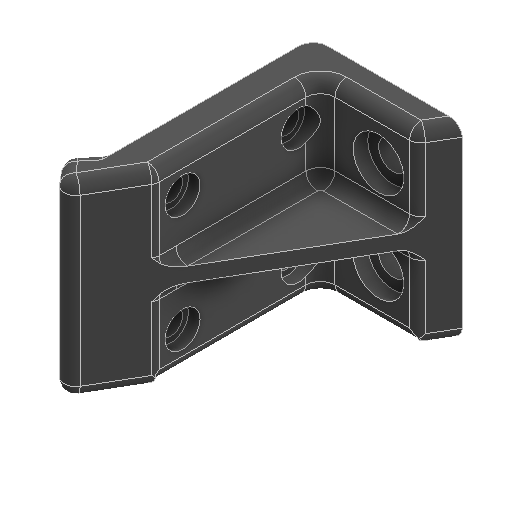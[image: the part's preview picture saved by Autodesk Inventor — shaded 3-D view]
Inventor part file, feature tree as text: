
AUTODESK INVENTOR PART (.ipt)
format: ipt  version: 2024.1 (Build 281209000, 209)  size: 401,920 bytes
history: native  units: in
note: dims shown in document units (in); Inventor stores cm internally (conversion verified against a paired STEP export)
features: sketch x4, other x3, plane x1
ambient origin geometry x8: Origin, YZ Plane, XZ Plane, XY Plane, X Axis, Y Axis, Z Axis, Center Point
bodies: Solid1 (feature_tree)
feature tree (8):
  other  "Motor Mounts.ipt"
  other  "Solid1::Motor Mounts.ipt"
  other  "TaggingFeature1"
  sketch  "Sketch1"  dims[d0=0.3937in]
  sketch  "Sketch2"  dims[d1=0.12in]
  sketch  "Sketch3"
  sketch  "Sketch4"
  plane  "Work Plane1"
